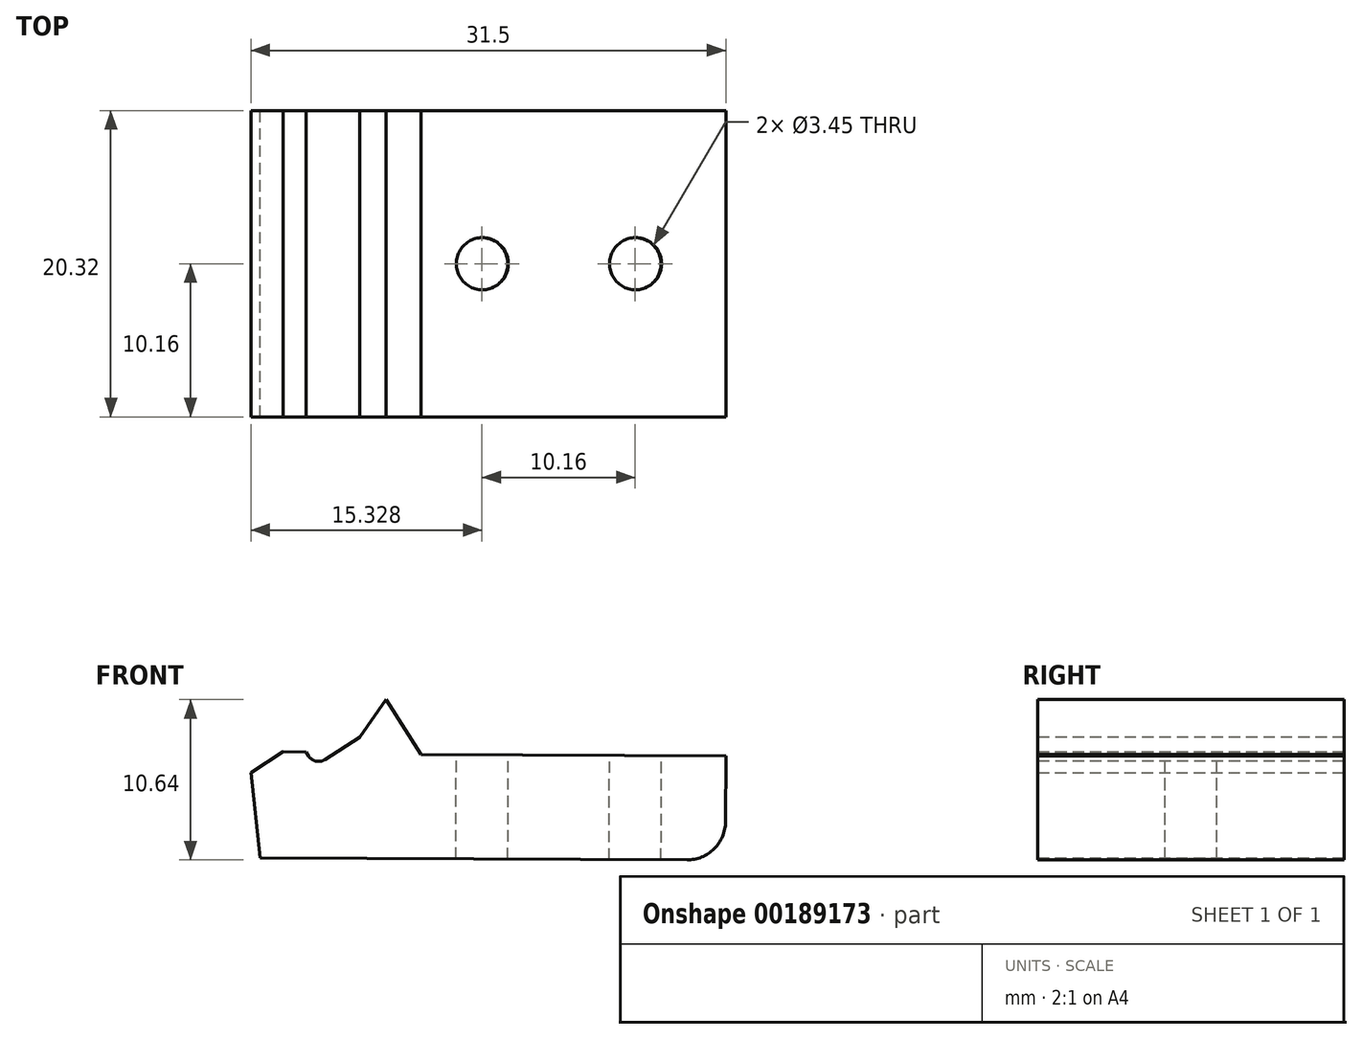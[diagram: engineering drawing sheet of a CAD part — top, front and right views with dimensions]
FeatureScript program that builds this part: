
annotation { "Feature Type Name" : "Feature", "Feature Type Description" : "" }
export const myFeature = defineFeature(function(context is Context, id is Id, definition is map)
    precondition{}
    {
        {
            var Q0;
            Q0=qCreatedBy(makeId("Front.planeOp"),FACE);
            var sketch = newSketch(context, id + "F0", { "sketchPlane" : qUnion([Q0])});
            skLineSegment(sketch, "E0", {"start": v(0, 0) * mm, "end": v(0, 29.21) * mm});
            skLineSegment(sketch, "E1", {"start": v(0, 0) * mm, "end": v(-10.16, 0) * mm});
            skLineSegment(sketch, "E2", {"start": v(-10.16, 0) * mm, "end": v(-10.16, 44.96) * mm});
            skLineSegment(sketch, "E3.0", {"start": v(0, 44.96) * mm, "end": v(12.7, 44.96) * mm});
            skLineSegment(sketch, "E4", {"start": v(0, 44.96) * mm, "end": v(0, 44.96) * mm});
            skLineSegment(sketch, "E5", {"start": v(0, 44.96) * mm, "end": v(-10.16, 44.96) * mm});
            skCircle(sketch, "E6", {"center": v(-5.08, 5.08) * mm, "radius": 1.73 * mm});
            skLineSegment(sketch, "E7", {"start": v(10.16, 39.88) * mm, "end": v(12.7, 44.96) * mm});
            skLineSegment(sketch, "E8", {"start": v(10.16, 39.88) * mm, "end": v(6.35, 39.88) * mm});
            skLineSegment(sketch, "E9", {"start": v(6.35, 39.88) * mm, "end": v(6.35, 41.8) * mm});
            skLineSegment(sketch, "E10", {"start": v(6.35, 41.8) * mm, "end": v(0, 41.8) * mm});
            skLineSegment(sketch, "E11", {"start": v(0, 41.8) * mm, "end": v(0, 29.21) * mm});
            skLineSegment(sketch, "E12", {"start": v(0, 44.96) * mm, "end": v(-23.22, 60.03) * mm});
            skLineSegment(sketch, "E13", {"start": v(-23.22, 60.03) * mm, "end": v(-29.56, 50.26) * mm});
            skLineSegment(sketch, "E14", {"start": v(-29.56, 50.26) * mm, "end": v(-10.16, 37.67) * mm});
            skSolve(sketch);
        }
        {
            var Q0;
            Q0=qSketchRegion(id+"F0",true);
            extrude(context, id + "F1", {"entities" : qUnion([Q0]), "endBound" : BoundingType.SYMMETRIC, "depth" : 58.42 * mm});
        }
        {
            var Q0;
            Q0=makeQuery(id+"F1.opExtrude","SWEPT_FACE",FACE,{"disambiguationData":[OSD([sQuery(id+"F0.wireOp",EDGE,"E0")])]});
            var sketch = newSketch(context, id + "F2", { "sketchPlane" : qUnion([Q0])});
            skLineSegment(sketch, "E15.bottom", {"start": v(23.37, 0) * mm, "end": v(-23.37, 0) * mm});
            skLineSegment(sketch, "E15.top", {"start": v(23.37, 40.64) * mm, "end": v(-23.37, 40.64) * mm});
            skLineSegment(sketch, "E15.left", {"start": v(23.37, 0) * mm, "end": v(23.37, 40.64) * mm});
            skLineSegment(sketch, "E15.right", {"start": v(-23.37, 0) * mm, "end": v(-23.37, 40.64) * mm});
            skSolve(sketch);
        }
        {
            var Q0;
            Q0=qSketchRegion(id+"F2",true);
            extrude(context, id + "F3", {"entities" : qUnion([Q0]), "operationType" : NewBodyOperationType.REMOVE, "oppositeDirection" : true, "depth" : 25.4 * mm});
        }
        {
            var Q0;
            Q0=makeQuery(id+"F1.opExtrude","CAP_FACE",FACE,{"disambiguationData":[OSD([sQuery(id+"F0.wireOp",EDGE,"E0"),sQuery(id+"F0.wireOp",EDGE,"E1"),sQuery(id+"F0.wireOp",EDGE,"E2"),sQuery(id+"F0.wireOp",EDGE,"prlR2u4p-7zGr-8wLY-PFS4-xYLywOnrNjr2"),sQuery(id+"F0.wireOp",EDGE,"E3.0"),sQuery(id+"F0.wireOp",EDGE,"42871ac2-c2a0-4b02-a882-5850723046cd"),sQuery(id+"F0.wireOp",EDGE,"E4"),sQuery(id+"F0.wireOp",EDGE,"E5"),sQuery(id+"F0.wireOp",EDGE,"RHK7HEwf-QzFp-As4H-Efqg-lgAJ1mc47Qq8"),sQuery(id+"F0.wireOp",EDGE,"HXlg5Q3d-pPcC-TzpV-dLrH-71LZfTlpnH6i"),sQuery(id+"F0.wireOp",EDGE,"39f0aba3-21ac-4e95-b7d3-faf603e52d2f"),sQuery(id+"F0.wireOp",EDGE,"E6")])],"isStart":true});
            var sketch = newSketch(context, id + "F4", { "sketchPlane" : qUnion([Q0])});
            skLineSegment(sketch, "E16.bottom", {"start": v(0, 38.6) * mm, "end": v(-15.24, 38.6) * mm});
            skLineSegment(sketch, "E16.top", {"start": v(0, 44.96) * mm, "end": v(-15.24, 44.96) * mm});
            skLineSegment(sketch, "E16.left", {"start": v(0, 38.6) * mm, "end": v(0, 44.96) * mm});
            skLineSegment(sketch, "E16.right", {"start": v(-15.24, 38.6) * mm, "end": v(-15.24, 44.96) * mm});
            skSolve(sketch);
        }
        {
            var Q0;
            Q0=qSketchRegion(id+"F4",true);
            extrude(context, id + "F5", {"entities" : qUnion([Q0]), "operationType" : NewBodyOperationType.REMOVE, "oppositeDirection" : true, "depth" : 19.05 * mm});
        }
        {
            var Q0;
            Q0=makeQuery(id+"F1.opExtrude","CAP_FACE",FACE,{"disambiguationData":[OSD([sQuery(id+"F0.wireOp",EDGE,"E0"),sQuery(id+"F0.wireOp",EDGE,"E1"),sQuery(id+"F0.wireOp",EDGE,"E2"),sQuery(id+"F0.wireOp",EDGE,"prlR2u4p-7zGr-8wLY-PFS4-xYLywOnrNjr2"),sQuery(id+"F0.wireOp",EDGE,"E3.0"),sQuery(id+"F0.wireOp",EDGE,"42871ac2-c2a0-4b02-a882-5850723046cd"),sQuery(id+"F0.wireOp",EDGE,"E5"),sQuery(id+"F0.wireOp",EDGE,"RHK7HEwf-QzFp-As4H-Efqg-lgAJ1mc47Qq8"),sQuery(id+"F0.wireOp",EDGE,"HXlg5Q3d-pPcC-TzpV-dLrH-71LZfTlpnH6i"),sQuery(id+"F0.wireOp",EDGE,"39f0aba3-21ac-4e95-b7d3-faf603e52d2f"),sQuery(id+"F0.wireOp",EDGE,"E6")])],"isStart":false});
            var sketch = newSketch(context, id + "F6", { "sketchPlane" : qUnion([Q0])});
            skLineSegment(sketch, "E17.bottom", {"start": v(0, 38.6) * mm, "end": v(15.24, 38.6) * mm});
            skLineSegment(sketch, "E17.top", {"start": v(0, 44.96) * mm, "end": v(15.24, 44.96) * mm});
            skLineSegment(sketch, "E17.left", {"start": v(0, 38.6) * mm, "end": v(0, 44.96) * mm});
            skLineSegment(sketch, "E17.right", {"start": v(15.24, 38.6) * mm, "end": v(15.24, 44.96) * mm});
            skSolve(sketch);
        }
        {
            var Q0;
            Q0=qSketchRegion(id+"F6",true);
            extrude(context, id + "F7", {"entities" : qUnion([Q0]), "operationType" : NewBodyOperationType.REMOVE, "oppositeDirection" : true, "depth" : 19.05 * mm});
        }
        {
            var Q0;
            Q0=makeQuery(id+"F7.boolean.opBoolean","COPY",FACE,{"derivedFrom":makeQuery(id+"F7.opExtrude","CAP_FACE",FACE,{"disambiguationData":[OSD([sQuery(id+"F6.wireOp",EDGE,"E17.bottom"),sQuery(id+"F6.wireOp",EDGE,"E17.top"),sQuery(id+"F6.wireOp",EDGE,"E17.left"),sQuery(id+"F6.wireOp",EDGE,"E17.right")])],"isStart":false})});
            var sketch = newSketch(context, id + "F8", { "sketchPlane" : qUnion([Q0])});
            skLineSegment(sketch, "E18", {"start": v(0, 41.8) * mm, "end": v(0, 40.64) * mm});
            skLineSegment(sketch, "E19", {"start": v(0, 40.64) * mm, "end": v(2.82, 41.8) * mm});
            skLineSegment(sketch, "E20", {"start": v(2.82, 41.8) * mm, "end": v(0, 41.8) * mm});
            skSolve(sketch);
        }
        {
            var Q0;
            Q0=qSketchRegion(id+"F8",true);
            extrude(context, id + "F9", {"entities" : qUnion([Q0]), "operationType" : NewBodyOperationType.ADD, "oppositeDirection" : true, "depth" : 20.32 * mm});
        }
        {
            var Q0;
            Q0=qCreatedBy(makeId("Front.planeOp"),FACE);
            var sketch = newSketch(context, id + "F10", { "sketchPlane" : qUnion([Q0])});
            skLineSegment(sketch, "E21", {"start": v(12.7, 44.96) * mm, "end": v(0, 44.96) * mm});
            skLineSegment(sketch, "E22", {"start": v(12.7, 44.96) * mm, "end": v(-13.18, 61.76) * mm});
            skLineSegment(sketch, "E23", {"start": v(-16.95, 55.96) * mm, "end": v(0, 44.96) * mm});
            skLineSegment(sketch, "E24", {"start": v(-16.95, 55.96) * mm, "end": v(-13.18, 61.76) * mm});
            skSolve(sketch);
        }
        {
            var Q0;
            Q0=qSketchRegion(id+"F10",true);
            extrude(context, id + "F11", {"entities" : qUnion([Q0]), "operationType" : NewBodyOperationType.ADD, "endBound" : BoundingType.SYMMETRIC, "depth" : 20.32 * mm});
        }
        {
            var Q0;
            Q0=makeQuery(id+"F1.opExtrude","SWEPT_EDGE",EDGE,{"disambiguationData":[OSD([sQuery(id+"F0.wireOp",EDGE,"E8"),sQuery(id+"F0.wireOp",EDGE,"E9")])]});
            chamfer(context, id + "F12", {"entities" : qUnion([Q0]), "chamferType" : ChamferType.OFFSET_ANGLE, "width" : 1.27 * mm, "oppositeDirection" : false, "angle" : 33 * degree, "tangentPropagation" : true});
        }
        {
            var Q0;
            Q0=makeQuery(id+"F1.opExtrude","SWEPT_FACE",FACE,{"disambiguationData":[OSD([sQuery(id+"F0.wireOp",EDGE,"E13")])]});
            var sketch = newSketch(context, id + "F13", { "sketchPlane" : qUnion([Q0])});
            skLineSegment(sketch, "E25.bottom", {"start": v(-12.7, 37.71) * mm, "end": v(12.7, 37.71) * mm});
            skLineSegment(sketch, "E25.top", {"start": v(-12.7, 26.06) * mm, "end": v(12.7, 26.06) * mm});
            skLineSegment(sketch, "E25.left", {"start": v(-12.7, 37.71) * mm, "end": v(-12.7, 26.06) * mm});
            skLineSegment(sketch, "E25.right", {"start": v(12.7, 37.71) * mm, "end": v(12.7, 26.06) * mm});
            skSolve(sketch);
        }
        {
            var Q0;
            Q0=qSketchRegion(id+"F13",true);
            extrude(context, id + "F14", {"entities" : qUnion([Q0]), "operationType" : NewBodyOperationType.ADD, "depth" : 38.1 * mm});
        }
        {
            var Q0;
            Q0=makeQuery(id+"F11.opExtrude","SWEPT_EDGE",EDGE,{"disambiguationData":[OSD([sQuery(id+"F10.wireOp",EDGE,"E22"),sQuery(id+"F10.wireOp",EDGE,"E24")])]});
            fillet(context, id + "F15", {"entities" : qUnion([Q0]), "radius" : 2.54 * mm, "tangentPropagation" : true, "allowEdgeOverflow" : false});
        }
        {
            var Q0;
            Q0=makeQuery(id+"F14.opExtrude","CAP_EDGE",EDGE,{"disambiguationData":[OSD([sQuery(id+"F13.wireOp",EDGE,"E25.right")])],"isStart":true});
            var Q1;
            Q1=makeQuery(id+"F14.opExtrude","CAP_EDGE",EDGE,{"disambiguationData":[OSD([sQuery(id+"F13.wireOp",EDGE,"E25.left")])],"isStart":true});
            var Q2;
            Q2=makeQuery(id+"F14.opExtrude","CAP_EDGE",EDGE,{"disambiguationData":[OSD([sQuery(id+"F13.wireOp",EDGE,"E25.left")])],"isStart":false});
            var Q3;
            Q3=makeQuery(id+"F14.opExtrude","CAP_EDGE",EDGE,{"disambiguationData":[OSD([sQuery(id+"F13.wireOp",EDGE,"E25.right")])],"isStart":false});
            fillet(context, id + "F16", {"entities" : qUnion([Q0, Q1, Q2, Q3]), "radius" : 6.35 * mm, "tangentPropagation" : true, "allowEdgeOverflow" : false});
        }
        {
            var Q0;
            Q0=makeQuery(id+"F1.opExtrude","SWEPT_EDGE",EDGE,{"disambiguationData":[OSD([sQuery(id+"F0.wireOp",EDGE,"E9"),sQuery(id+"F0.wireOp",EDGE,"E10")])]});
            fillet(context, id + "F17", {"entities" : qUnion([Q0]), "radius" : 0.8 * mm, "tangentPropagation" : true, "allowEdgeOverflow" : false});
        }
        {
            var Q0;
            Q0=makeQuery(id+"F1.opExtrude","CAP_FACE",FACE,{"disambiguationData":[OSD([sQuery(id+"F0.wireOp",EDGE,"E0"),sQuery(id+"F0.wireOp",EDGE,"E1"),sQuery(id+"F0.wireOp",EDGE,"E2"),sQuery(id+"F0.wireOp",EDGE,"E3.0"),sQuery(id+"F0.wireOp",EDGE,"E6"),sQuery(id+"F0.wireOp",EDGE,"E7"),sQuery(id+"F0.wireOp",EDGE,"E8"),sQuery(id+"F0.wireOp",EDGE,"E9"),sQuery(id+"F0.wireOp",EDGE,"E10"),sQuery(id+"F0.wireOp",EDGE,"E11"),sQuery(id+"F0.wireOp",EDGE,"E12"),sQuery(id+"F0.wireOp",EDGE,"E13"),sQuery(id+"F0.wireOp",EDGE,"E14")])],"isStart":false});
            var sketch = newSketch(context, id + "F18", { "sketchPlane" : qUnion([Q0])});
            skLineSegment(sketch, "E26", {"start": v(-29.56, 50.26) * mm, "end": v(-10.16, 0) * mm});
            skSolve(sketch);
        }
        {
            var Q0;
            Q0=qSketchRegion(id+"F18",true);
            var Q1;
            Q1=makeQuery(id+"F18.imprint","IMPRINT",FACE,{"disambiguationData":[TD([[makeQuery(id+"F18.imprint","IMPRINT",EDGE,{"derivedFrom":sQuery(id+"F18.wireOp",EDGE,"E26")}),1.0]])]});
            extrude(context, id + "F19", {"entities" : qUnion([Q0, Q1]), "operationType" : NewBodyOperationType.ADD, "oppositeDirection" : true, "depth" : 5.84 * mm});
        }
        {
            var Q0;
            Q0=makeQuery(id+"F1.opExtrude","CAP_FACE",FACE,{"disambiguationData":[OSD([sQuery(id+"F0.wireOp",EDGE,"E0"),sQuery(id+"F0.wireOp",EDGE,"E1"),sQuery(id+"F0.wireOp",EDGE,"E2"),sQuery(id+"F0.wireOp",EDGE,"E3.0"),sQuery(id+"F0.wireOp",EDGE,"E6"),sQuery(id+"F0.wireOp",EDGE,"E7"),sQuery(id+"F0.wireOp",EDGE,"E8"),sQuery(id+"F0.wireOp",EDGE,"E9"),sQuery(id+"F0.wireOp",EDGE,"E10"),sQuery(id+"F0.wireOp",EDGE,"E11"),sQuery(id+"F0.wireOp",EDGE,"E12"),sQuery(id+"F0.wireOp",EDGE,"E13"),sQuery(id+"F0.wireOp",EDGE,"E14")])],"isStart":true});
            var sketch = newSketch(context, id + "F20", { "sketchPlane" : qUnion([Q0])});
            skLineSegment(sketch, "E27", {"start": v(29.56, 50.26) * mm, "end": v(10.16, 0) * mm});
            skSolve(sketch);
        }
        {
            var Q0;
            Q0=makeQuery(id+"F20.imprint","IMPRINT",FACE,{"disambiguationData":[TD([[makeQuery(id+"F20.imprint","IMPRINT",EDGE,{"derivedFrom":sQuery(id+"F20.wireOp",EDGE,"E27")}),-1.0]])]});
            extrude(context, id + "F21", {"entities" : qUnion([Q0]), "operationType" : NewBodyOperationType.ADD, "oppositeDirection" : true, "depth" : 5.84 * mm});
        }
        {
            var Q0;
            {var subQ0=sQuery(id+"F0.wireOp",EDGE,"E0");var subQ1=sQuery(id+"F0.wireOp",EDGE,"E1");Q0=makeQuery(id+"F3.boolean.opBoolean","SPLIT",EDGE,{"disambiguationData":[TD([makeQuery(id+"F3.opExtrude","SWEPT_FACE",FACE,{"disambiguationData":[OSD([sQuery(id+"F2.wireOp",EDGE,"E15.right")])]})])],"derivedFrom":makeQuery(id+"F1.opExtrude","SWEPT_EDGE",EDGE,{"disambiguationData":[OSD([subQ0,subQ1])]})});}
            var Q1;
            {var subQ0=sQuery(id+"F0.wireOp",EDGE,"E0");var subQ1=sQuery(id+"F0.wireOp",EDGE,"E1");Q1=makeQuery(id+"F3.boolean.opBoolean","SPLIT",EDGE,{"disambiguationData":[TD([makeQuery(id+"F3.opExtrude","SWEPT_FACE",FACE,{"disambiguationData":[OSD([sQuery(id+"F2.wireOp",EDGE,"E15.left")])]})])],"derivedFrom":makeQuery(id+"F1.opExtrude","SWEPT_EDGE",EDGE,{"disambiguationData":[OSD([subQ0,subQ1])]})});}
            var Q2;
            {var subQ0=sQuery(id+"F0.wireOp",EDGE,"E2");var subQ1=sQuery(id+"F0.wireOp",EDGE,"E1");Q2=makeQuery(id+"F3.boolean.opBoolean","SPLIT",EDGE,{"disambiguationData":[TD([makeQuery(id+"F3.opExtrude","SWEPT_FACE",FACE,{"disambiguationData":[OSD([sQuery(id+"F2.wireOp",EDGE,"E15.right")])]})])],"derivedFrom":makeQuery(id+"F1.opExtrude","SWEPT_EDGE",EDGE,{"disambiguationData":[OSD([subQ1,subQ0])]})});}
            var Q3;
            {var subQ0=sQuery(id+"F0.wireOp",EDGE,"E2");var subQ1=sQuery(id+"F0.wireOp",EDGE,"E1");Q3=makeQuery(id+"F3.boolean.opBoolean","SPLIT",EDGE,{"disambiguationData":[TD([makeQuery(id+"F3.opExtrude","SWEPT_FACE",FACE,{"disambiguationData":[OSD([sQuery(id+"F2.wireOp",EDGE,"E15.left")])]})])],"derivedFrom":makeQuery(id+"F1.opExtrude","SWEPT_EDGE",EDGE,{"disambiguationData":[OSD([subQ1,subQ0])]})});}
            fillet(context, id + "F22", {"entities" : qUnion([Q0, Q1, Q2, Q3]), "radius" : 3.8 * mm, "tangentPropagation" : true, "allowEdgeOverflow" : false});
        }
        {
            var Q0;
            Q0=makeQuery(id+"F21.boolean.opBoolean","MERGE",FACE,{"derivedFrom":[makeQuery(id+"F3.boolean.opBoolean","COPY",FACE,{"derivedFrom":makeQuery(id+"F3.opExtrude","SWEPT_FACE",FACE,{"disambiguationData":[OSD([sQuery(id+"F2.wireOp",EDGE,"E15.left")])]})}),makeQuery(id+"F21.opExtrude","CAP_FACE",FACE,{"disambiguationData":[OSD([sQuery(id+"F0.wireOp",EDGE,"E2"),sQuery(id+"F0.wireOp",EDGE,"E14"),sQuery(id+"F20.wireOp",EDGE,"E27")])],"isStart":false})]});
            var sketch = newSketch(context, id + "F23", { "sketchPlane" : qUnion([Q0])});
            skLineSegment(sketch, "E28", {"start": v(-14.74, 40.64) * mm, "end": v(-5.48, 34.63) * mm});
            skLineSegment(sketch, "E29", {"start": v(-5.48, 34.63) * mm, "end": v(0, 40.64) * mm});
            skLineSegment(sketch, "E30", {"start": v(0, 40.64) * mm, "end": v(-14.74, 40.64) * mm});
            skSolve(sketch);
        }
        {
            var Q0;
            Q0=makeQuery(id+"F23.imprint","IMPRINT",FACE,{"disambiguationData":[TD([[makeQuery(id+"F23.imprint","IMPRINT",EDGE,{"derivedFrom":sQuery(id+"F23.wireOp",EDGE,"E28")}),1.0]])]});
            extrude(context, id + "F24", {"entities" : qUnion([Q0]), "operationType" : NewBodyOperationType.ADD, "depth" : 46.74 * mm});
        }
        {
            var Q0;
            Q0=makeQuery(id+"F24.boolean.opBoolean","MERGE",FACE,{"derivedFrom":[makeQuery(id+"F14.boolean.opBoolean","MERGE",FACE,{"derivedFrom":[makeQuery(id+"F1.opExtrude","SWEPT_FACE",FACE,{"disambiguationData":[OSD([sQuery(id+"F0.wireOp",EDGE,"E14")])]}),makeQuery(id+"F14.opExtrude","SWEPT_FACE",FACE,{"disambiguationData":[OSD([sQuery(id+"F13.wireOp",EDGE,"E25.top")])]})]}),makeQuery(id+"F24.opExtrude","SWEPT_FACE",FACE,{"disambiguationData":[OSD([sQuery(id+"F23.wireOp",EDGE,"E28")])]})]});
            var sketch = newSketch(context, id + "F25", { "sketchPlane" : qUnion([Q0])});
            skCircle(sketch, "E31", {"center": v(-28.53, 0) * mm, "radius": 1.73 * mm});
            skCircle(sketch, "E32", {"center": v(-38.7, 0) * mm, "radius": 1.73 * mm});
            skSolve(sketch);
        }
        {
            var Q0;
            Q0=makeQuery(id+"F25.imprint","IMPRINT",FACE,{"disambiguationData":[TD([[makeQuery(id+"F25.imprint","IMPRINT",EDGE,{"derivedFrom":sQuery(id+"F25.wireOp",EDGE,"E31")}),1.0]])]});
            var Q1;
            Q1=makeQuery(id+"F25.imprint","IMPRINT",FACE,{"disambiguationData":[TD([[makeQuery(id+"F25.imprint","IMPRINT",EDGE,{"derivedFrom":sQuery(id+"F25.wireOp",EDGE,"E32")}),1.0]])]});
            extrude(context, id + "F26", {"entities" : qUnion([Q0, Q1]), "operationType" : NewBodyOperationType.REMOVE, "endBound" : BoundingType.THROUGH_ALL, "oppositeDirection" : true, "depth" : 25.4 * mm});
        }
        {
            var Q0;
            {var subQ0=sQuery(id+"F0.wireOp",EDGE,"E14");var subQ1=sQuery(id+"F0.wireOp",EDGE,"E2");Q0=makeQuery(id+"F19.boolean.opBoolean","MERGE",FACE,{"derivedFrom":[makeQuery(id+"F1.opExtrude","CAP_FACE",FACE,{"disambiguationData":[OSD([sQuery(id+"F0.wireOp",EDGE,"E0"),sQuery(id+"F0.wireOp",EDGE,"E1"),subQ1,sQuery(id+"F0.wireOp",EDGE,"E3.0"),sQuery(id+"F0.wireOp",EDGE,"E6"),sQuery(id+"F0.wireOp",EDGE,"E7"),sQuery(id+"F0.wireOp",EDGE,"E8"),sQuery(id+"F0.wireOp",EDGE,"E9"),sQuery(id+"F0.wireOp",EDGE,"E10"),sQuery(id+"F0.wireOp",EDGE,"E11"),sQuery(id+"F0.wireOp",EDGE,"E12"),sQuery(id+"F0.wireOp",EDGE,"E13"),subQ0])],"isStart":false}),makeQuery(id+"F19.opExtrude","CAP_FACE",FACE,{"disambiguationData":[OSD([subQ1,subQ0,sQuery(id+"F18.wireOp",EDGE,"E26")])],"isStart":true})]});}
            var sketch = newSketch(context, id + "F27", { "sketchPlane" : qUnion([Q0])});
            skLineSegment(sketch, "E33", {"start": v(0, 44.96) * mm, "end": v(-63.45, 86.14) * mm});
            skLineSegment(sketch, "E34", {"start": v(-63.45, 86.14) * mm, "end": v(-78.14, 63.52) * mm});
            skLineSegment(sketch, "E35", {"start": v(-78.14, 63.52) * mm, "end": v(-38.56, 36.37) * mm});
            skLineSegment(sketch, "E36", {"start": v(-38.56, 36.37) * mm, "end": v(-20.24, -3.19) * mm});
            skLineSegment(sketch, "E37", {"start": v(-20.24, -3.19) * mm, "end": v(0, -3.19) * mm});
            skLineSegment(sketch, "E38", {"start": v(0, -3.19) * mm, "end": v(0, 44.96) * mm});
            skSolve(sketch);
        }
        {
            var Q0;
            Q0 = qSketchRegion(id + "F27", true);
            extrude(context, id + "F28", {"entities" : qUnion([Q0]), "operationType" : NewBodyOperationType.REMOVE, "oppositeDirection" : true, "depth" : 76.2 * mm});
        }
        {
            var Q0;
            Q0=makeQuery(id+"F1.opExtrude","SWEPT_BODY",BODY,{"disambiguationData":[OSD([sQuery(id+"F0.wireOp",EDGE,"E0"),sQuery(id+"F0.wireOp",EDGE,"E1"),sQuery(id+"F0.wireOp",EDGE,"E2"),sQuery(id+"F0.wireOp",EDGE,"E3.0"),sQuery(id+"F0.wireOp",EDGE,"E6"),sQuery(id+"F0.wireOp",EDGE,"E7"),sQuery(id+"F0.wireOp",EDGE,"E8"),sQuery(id+"F0.wireOp",EDGE,"E9"),sQuery(id+"F0.wireOp",EDGE,"E10"),sQuery(id+"F0.wireOp",EDGE,"E11"),sQuery(id+"F0.wireOp",EDGE,"E12"),sQuery(id+"F0.wireOp",EDGE,"E13"),sQuery(id+"F0.wireOp",EDGE,"E14")])]});
            var Q1;
            Q1=makeQuery(id+"F11.boolean.opBoolean","MERGE",EDGE,{"derivedFrom":[makeQuery(id+"F1.opExtrude","SWEPT_EDGE",EDGE,{"disambiguationData":[OSD([sQuery(id+"F0.wireOp",EDGE,"E3.0"),sQuery(id+"F0.wireOp",EDGE,"E7")])]}),makeQuery(id+"F11.opExtrude","SWEPT_EDGE",EDGE,{"disambiguationData":[OSD([sQuery(id+"F10.wireOp",EDGE,"E21"),sQuery(id+"F10.wireOp",EDGE,"E22")])]})]});
            transform(context, id + "F29", {"entities" : qUnion([Q0]), "transformType" : TransformType.ROTATION, "transformAxis" : qUnion([Q1]), "angle" : 147.32 * degree, "makeCopy" : false});
        }
        {
            var Q0;
            Q0=makeQuery(id+"F1.opExtrude","SWEPT_BODY",BODY,{"disambiguationData":[OSD([sQuery(id+"F0.wireOp",EDGE,"E0"),sQuery(id+"F0.wireOp",EDGE,"E1"),sQuery(id+"F0.wireOp",EDGE,"E2"),sQuery(id+"F0.wireOp",EDGE,"E3.0"),sQuery(id+"F0.wireOp",EDGE,"E6"),sQuery(id+"F0.wireOp",EDGE,"E7"),sQuery(id+"F0.wireOp",EDGE,"E8"),sQuery(id+"F0.wireOp",EDGE,"E9"),sQuery(id+"F0.wireOp",EDGE,"E10"),sQuery(id+"F0.wireOp",EDGE,"E11"),sQuery(id+"F0.wireOp",EDGE,"E12"),sQuery(id+"F0.wireOp",EDGE,"E13"),sQuery(id+"F0.wireOp",EDGE,"E14")])]});
            transform(context, id + "F30", {"entities" : qUnion([Q0]), "transformType" : TransformType.TRANSLATION_3D, "dx" : -12.45 * mm, "dy" : 0 * mm, "dz" : -44.7 * mm, "makeCopy" : false});
        }
    });
